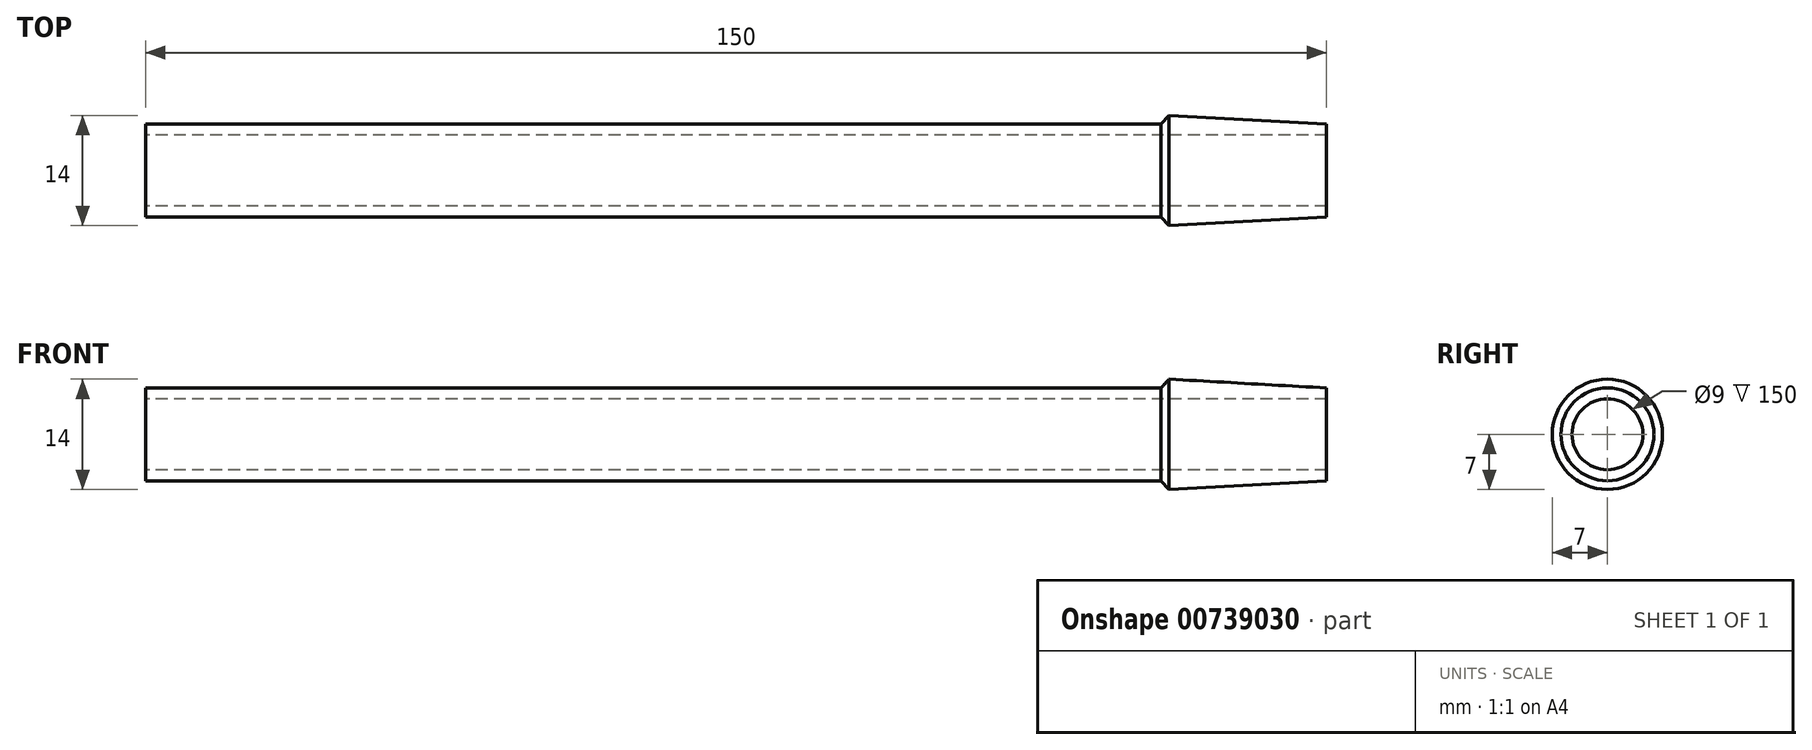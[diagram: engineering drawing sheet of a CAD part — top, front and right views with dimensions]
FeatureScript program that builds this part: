
annotation { "Feature Type Name" : "Feature", "Feature Type Description" : "" }
export const myFeature = defineFeature(function(context is Context, id is Id, definition is map)
    precondition{}
    {
        {
            var Q0;
            Q0=qCreatedBy(makeId("Front.planeOp"),FACE);
            var sketch = newSketch(context, id + "F0", { "sketchPlane" : qUnion([Q0])});
            skLineSegment(sketch, "E0.bottom", {"start": v(-75, -4.5) * mm, "end": v(75, -4.5) * mm, "construction": true});
            skLineSegment(sketch, "E0.top", {"start": v(-75, 4.5) * mm, "end": v(75, 4.5) * mm, "construction": true});
            skLineSegment(sketch, "E0.left", {"start": v(-75, -4.5) * mm, "end": v(-75, 4.5) * mm, "construction": true});
            skLineSegment(sketch, "E0.right", {"start": v(75, -4.5) * mm, "end": v(75, 4.5) * mm, "construction": true});
            skPoint(sketch, "E0.middle", {"position": v(0, 0) * mm});
            skLineSegment(sketch, "E1", {"start": v(-75, 4.5) * mm, "end": v(75, 4.5) * mm});
            skLineSegment(sketch, "E2", {"start": v(-75, 4.5) * mm, "end": v(-75, 5.9) * mm});
            skLineSegment(sketch, "E3", {"start": v(-75, 5.9) * mm, "end": v(55, 5.9) * mm});
            skLineSegment(sketch, "E4", {"start": v(55, 5.9) * mm, "end": v(55, 7) * mm});
            skLineSegment(sketch, "E5", {"start": v(55, 7) * mm, "end": v(75, 5.9) * mm});
            skLineSegment(sketch, "E6", {"start": v(75, 5.9) * mm, "end": v(75, 4.5) * mm});
            skLineSegment(sketch, "E7", {"start": v(55, 5.9) * mm, "end": v(75, 5.9) * mm, "construction": true});
            skLineSegment(sketch, "E8", {"start": v(-75, 0) * mm, "end": v(75, 0) * mm, "construction": true});
            skLineSegment(sketch, "E9", {"start": v(55, 7) * mm, "end": v(53.98, 5.9) * mm});
            skSolve(sketch);
        }
        {
            var Q0;
            Q0=makeQuery(id+"F0.imprint","IMPRINT",FACE,{"disambiguationData":[TD([[makeQuery(id+"F0.imprint","IMPRINT",EDGE,{"derivedFrom":sQuery(id+"F0.wireOp",EDGE,"E1")}),1.0]])]});
            var Q1;
            {var subQ0=sQuery(id+"F0.wireOp",EDGE,"E4");Q1=makeQuery(id+"F0.imprint","IMPRINT",FACE,{"disambiguationData":[TD([[makeQuery(id+"F0.imprint","IMPRINT",EDGE,{"derivedFrom":subQ0}),1.0]])]});}
            var Q2;
            Q2=sQuery(id+"F0.wireOp",EDGE,"E8");
            revolve(context, id + "F1", {"surfaceOperationType" : NewSurfaceOperationType.NEW, "entities" : qUnion([Q0, Q1]), "axis" : qUnion([Q2]), "revolveType" : RevolveType.FULL});
        }
    });
